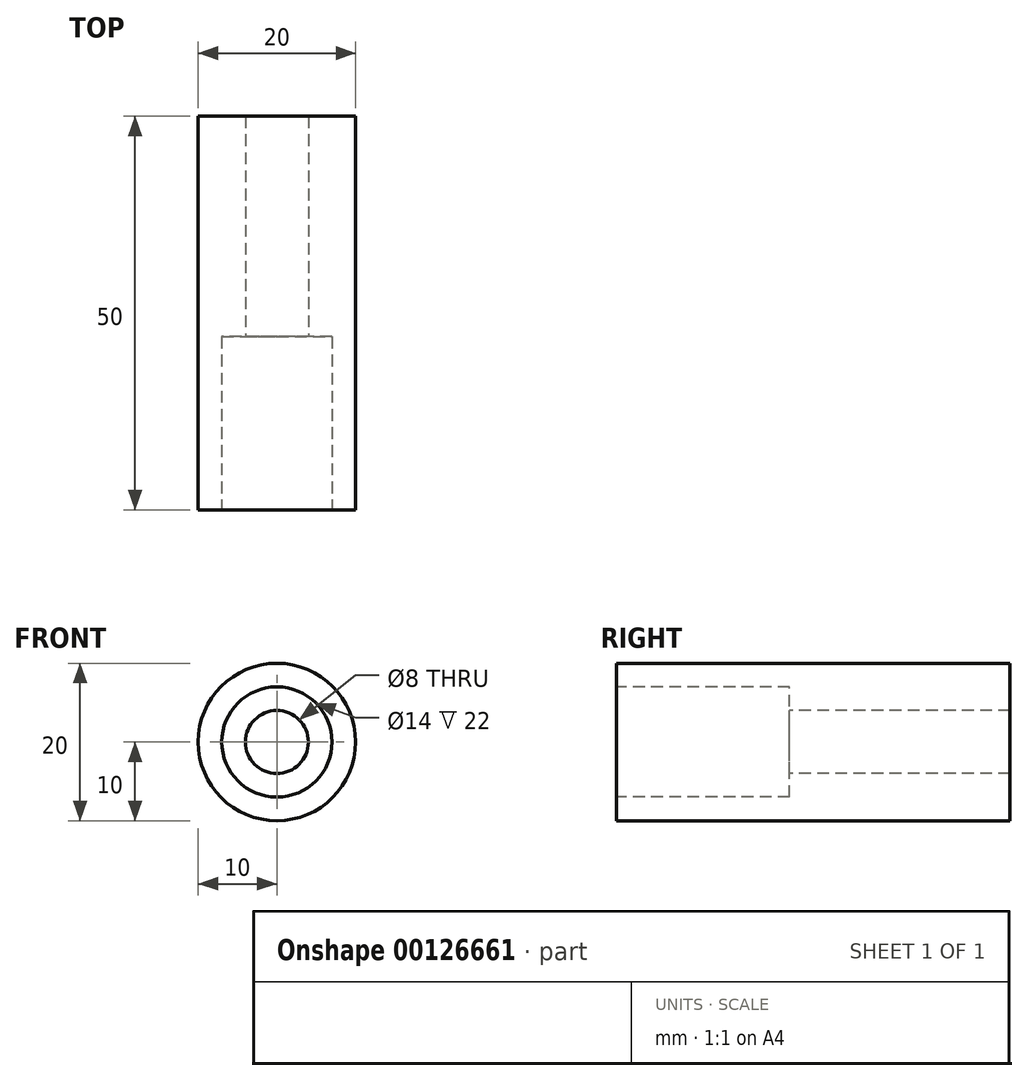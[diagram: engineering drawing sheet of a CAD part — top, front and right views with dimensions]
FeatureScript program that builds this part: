
annotation { "Feature Type Name" : "Feature", "Feature Type Description" : "" }
export const myFeature = defineFeature(function(context is Context, id is Id, definition is map)
    precondition{}
    {
        {
            var Q0;
            Q0=qCreatedBy(makeId("Front.planeOp"),FACE);
            var sketch = newSketch(context, id + "F0", { "sketchPlane" : qUnion([Q0])});
            skCircle(sketch, "E0", {"center": v(0, 0) * mm, "radius": 10 * mm});
            skSolve(sketch);
        }
        {
            var Q0;
            Q0 = qSketchRegion(id + "F0", true);
            extrude(context, id + "F1", {"entities" : qUnion([Q0]), "depth" : 50 * mm});
        }
        {
            var Q0;
            Q0=makeQuery(id+"F1.opExtrude","CAP_FACE",FACE,{"disambiguationData":[OSD([sQuery(id+"F0.wireOp",EDGE,"E0")])],"isStart":false});
            var sketch = newSketch(context, id + "F2", { "sketchPlane" : qUnion([Q0])});
            skCircle(sketch, "E1", {"center": v(0, 0) * mm, "radius": 4 * mm});
            skSolve(sketch);
        }
        {
            var Q0;
            Q0 = qSketchRegion(id + "F2", true);
            extrude(context, id + "F3", {"entities" : qUnion([Q0]), "operationType" : NewBodyOperationType.REMOVE, "oppositeDirection" : true, "depth" : 81.57 * mm});
        }
        {
            var Q0;
            Q0=makeQuery(id+"F1.opExtrude","CAP_FACE",FACE,{"disambiguationData":[OSD([sQuery(id+"F0.wireOp",EDGE,"E0")])],"isStart":false});
            var sketch = newSketch(context, id + "F4", { "sketchPlane" : qUnion([Q0])});
            skCircle(sketch, "E2", {"center": v(0, 0) * mm, "radius": 7 * mm});
            skSolve(sketch);
        }
        {
            var Q0;
            Q0 = qSketchRegion(id + "F4", true);
            extrude(context, id + "F5", {"entities" : qUnion([Q0]), "operationType" : NewBodyOperationType.REMOVE, "oppositeDirection" : true, "depth" : 22 * mm});
        }
    });
